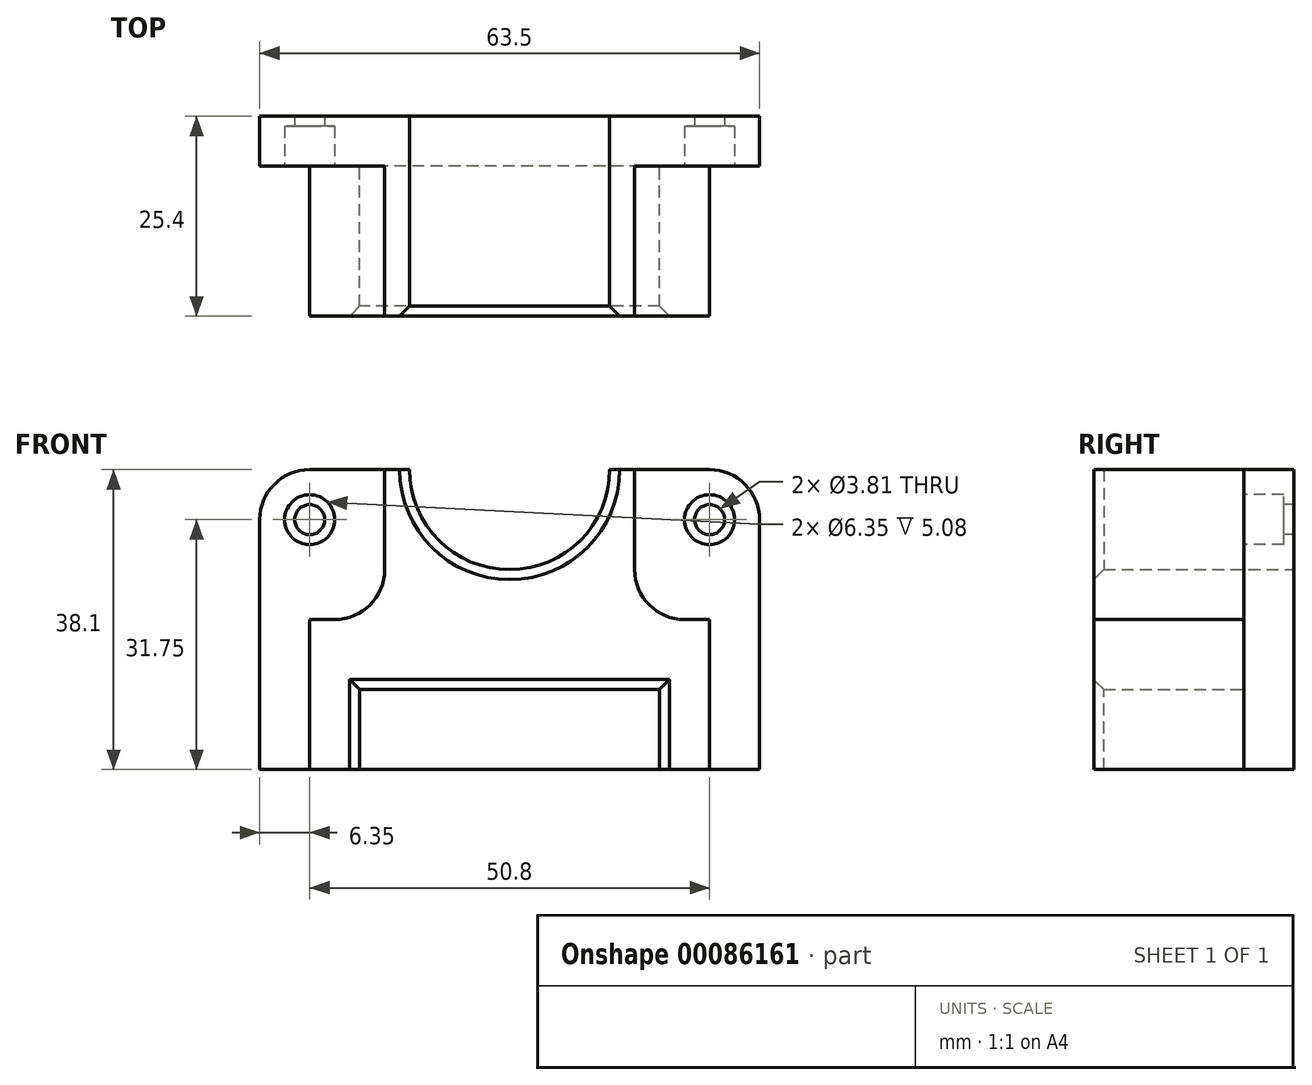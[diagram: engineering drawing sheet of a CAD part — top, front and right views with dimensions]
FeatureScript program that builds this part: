
annotation { "Feature Type Name" : "Feature", "Feature Type Description" : "" }
export const myFeature = defineFeature(function(context is Context, id is Id, definition is map)
    precondition{}
    {
        {
            var Q0;
            Q0=qCreatedBy(makeId("Front.planeOp"),FACE);
            var sketch = newSketch(context, id + "F0", { "sketchPlane" : qUnion([Q0])});
            skLineSegment(sketch, "E0.bottom", {"start": v(25.4, 19.05) * mm, "end": v(-25.4, 19.05) * mm});
            skLineSegment(sketch, "E0.top", {"start": v(31.75, -19.05) * mm, "end": v(-31.75, -19.05) * mm});
            skLineSegment(sketch, "E0.left", {"start": v(31.75, 12.7) * mm, "end": v(31.75, -19.05) * mm});
            skLineSegment(sketch, "E0.right", {"start": v(-31.75, 12.7) * mm, "end": v(-31.75, -19.05) * mm});
            skPoint(sketch, "E0.middle", {"position": v(0, 0) * mm});
            skPoint(sketch, "E1.visualSharp", {"position": v(31.75, 19.05) * mm});
            skArc(sketch, "E1.filletArc", {"start": v(31.75, 12.7) * mm, "mid": v(29.9, 17.2) * mm, "end": v(25.4, 19.05) * mm});
            skPoint(sketch, "E2.visualSharp", {"position": v(-31.75, 19.05) * mm});
            skArc(sketch, "E2.filletArc", {"start": v(-25.4, 19.05) * mm, "mid": v(-29.9, 17.2) * mm, "end": v(-31.75, 12.7) * mm});
            skSolve(sketch);
        }
        {
            var Q0;
            Q0=makeQuery(id+"F0.imprint","IMPRINT",FACE,{"disambiguationData":[TD([[makeQuery(id+"F0.imprint","IMPRINT",EDGE,{"derivedFrom":sQuery(id+"F0.wireOp",EDGE,"E0.bottom")}),1.0]])]});
            extrude(context, id + "F1", {"entities" : qUnion([Q0]), "depth" : 6.35 * mm});
        }
        {
            var Q0;
            Q0=makeQuery(id+"F1.opExtrude","CAP_FACE",FACE,{"disambiguationData":[OSD([sQuery(id+"F0.wireOp",EDGE,"E0.bottom"),sQuery(id+"F0.wireOp",EDGE,"E0.top"),sQuery(id+"F0.wireOp",EDGE,"E0.left"),sQuery(id+"F0.wireOp",EDGE,"E0.right")])],"isStart":false});
            var sketch = newSketch(context, id + "F2", { "sketchPlane" : qUnion([Q0])});
            skLineSegment(sketch, "E3.bottom", {"start": v(25.4, -19.05) * mm, "end": v(19.05, -19.05) * mm});
            skLineSegment(sketch, "E3.top", {"start": v(15.88, 19.05) * mm, "end": v(12.7, 19.05) * mm});
            skLineSegment(sketch, "E3.left", {"start": v(25.4, -19.05) * mm, "end": v(25.4, 0) * mm});
            skLineSegment(sketch, "E3.right", {"start": v(-25.4, -19.05) * mm, "end": v(-25.4, 0) * mm});
            skPoint(sketch, "E3.middle", {"position": v(0, 0) * mm});
            skLineSegment(sketch, "E4.top", {"start": v(19.05, -8.89) * mm, "end": v(-19.05, -8.9) * mm});
            skLineSegment(sketch, "E4.left", {"start": v(19.05, -19.05) * mm, "end": v(19.05, -8.89) * mm});
            skLineSegment(sketch, "E4.right", {"start": v(-19.05, -19.05) * mm, "end": v(-19.05, -8.9) * mm});
            skPoint(sketch, "E4.middle", {"position": v(0, -13.97) * mm});
            skArc(sketch, "E5", {"start": v(-12.7, 19.05) * mm, "mid": v(0, 6.35) * mm, "end": v(12.7, 19.05) * mm});
            skLineSegment(sketch, "E6.top", {"start": v(25.4, 0) * mm, "end": v(22.23, 0) * mm});
            skLineSegment(sketch, "E6.right", {"start": v(15.88, 19.05) * mm, "end": v(15.88, 6.35) * mm});
            skLineSegment(sketch, "E7.top", {"start": v(-25.4, 0) * mm, "end": v(-22.23, 0) * mm});
            skLineSegment(sketch, "E7.right", {"start": v(-15.88, 19.05) * mm, "end": v(-15.88, 6.35) * mm});
            skLineSegment(sketch, "E8.trimOffspring", {"start": v(-19.05, -19.05) * mm, "end": v(-25.4, -19.05) * mm});
            skPoint(sketch, "E9.orphan", {"position": v(25.4, 19.05) * mm});
            skPoint(sketch, "E10.orphan", {"position": v(-25.4, 19.05) * mm});
            skPoint(sketch, "E11.visualSharp", {"position": v(15.88, 0) * mm});
            skArc(sketch, "E11.filletArc", {"start": v(15.88, 6.35) * mm, "mid": v(17.73, 1.86) * mm, "end": v(22.23, 0) * mm});
            skPoint(sketch, "E12.visualSharp", {"position": v(-15.88, 0) * mm});
            skArc(sketch, "E12.filletArc", {"start": v(-22.23, 0) * mm, "mid": v(-17.73, 1.86) * mm, "end": v(-15.88, 6.35) * mm});
            skLineSegment(sketch, "E13.trimOffspring", {"start": v(-12.7, 19.05) * mm, "end": v(-15.87, 19.05) * mm});
            skSolve(sketch);
        }
        {
            var Q0;
            Q0 = qSketchRegion(id + "F2", true);
            extrude(context, id + "F3", {"entities" : qUnion([Q0]), "operationType" : NewBodyOperationType.ADD, "depth" : 19.05 * mm});
        }
        {
            var Q0;
            {var subQ0=sQuery(id+"F0.wireOp",EDGE,"E0.bottom");Q0=makeQuery(id+"F3.boolean.opBoolean","SPLIT",FACE,{"disambiguationData":[TD([makeQuery(id+"F3.opExtrude","SWEPT_FACE",FACE,{"disambiguationData":[OSD([sQuery(id+"F2.wireOp",EDGE,"E5")])]})])],"derivedFrom":makeQuery(id+"F1.opExtrude","CAP_FACE",FACE,{"disambiguationData":[OSD([subQ0,sQuery(id+"F0.wireOp",EDGE,"E0.top"),sQuery(id+"F0.wireOp",EDGE,"E0.left"),sQuery(id+"F0.wireOp",EDGE,"E0.right")])],"isStart":false})});}
            extrude(context, id + "F4", {"entities" : qUnion([Q0]), "operationType" : NewBodyOperationType.REMOVE, "endBound" : BoundingType.THROUGH_ALL, "oppositeDirection" : true, "depth" : 25.4 * mm});
        }
        {
            var Q0;
            Q0=makeQuery(id+"F3.opExtrude","CAP_EDGE",EDGE,{"disambiguationData":[OSD([sQuery(id+"F2.wireOp",EDGE,"E4.top")])],"isStart":false});
            var Q1;
            Q1=makeQuery(id+"F3.opExtrude","CAP_EDGE",EDGE,{"disambiguationData":[OSD([sQuery(id+"F2.wireOp",EDGE,"E4.right")])],"isStart":false});
            var Q2;
            Q2=makeQuery(id+"F3.opExtrude","CAP_EDGE",EDGE,{"disambiguationData":[OSD([sQuery(id+"F2.wireOp",EDGE,"E4.left")])],"isStart":false});
            chamfer(context, id + "F5", {"entities" : qUnion([Q0, Q1, Q2]), "width" : 1.27 * mm, "tangentPropagation" : true});
        }
        {
            var Q0;
            Q0=makeQuery(id+"F3.opExtrude","CAP_EDGE",EDGE,{"disambiguationData":[OSD([sQuery(id+"F2.wireOp",EDGE,"E5")])],"isStart":false});
            chamfer(context, id + "F6", {"entities" : qUnion([Q0]), "width" : 1.27 * mm, "tangentPropagation" : true});
        }
        {
            var Q0;
            {var subQ0=sQuery(id+"F0.wireOp",EDGE,"E0.bottom");var subQ1=sQuery(id+"F0.wireOp",EDGE,"E0.top");var subQ2=sQuery(id+"F0.wireOp",EDGE,"E0.right");var subQ3=sQuery(id+"F0.wireOp",EDGE,"E2.filletArc");Q0=makeQuery(id+"F3.boolean.opBoolean","SPLIT",FACE,{"disambiguationData":[TD([makeQuery(id+"F1.opExtrude","SWEPT_FACE",FACE,{"disambiguationData":[OSD([subQ2])]})])],"derivedFrom":makeQuery(id+"F1.opExtrude","CAP_FACE",FACE,{"disambiguationData":[OSD([subQ0,subQ1,sQuery(id+"F0.wireOp",EDGE,"E0.left"),subQ2,sQuery(id+"F0.wireOp",EDGE,"E1.filletArc"),subQ3])],"isStart":false})});}
            var sketch = newSketch(context, id + "F7", { "sketchPlane" : qUnion([Q0])});
            skPoint(sketch, "E14", {"position": v(-25.4, 12.7) * mm});
            skSolve(sketch);
        }
        {
            var Q0;
            {var subQ0=sQuery(id+"F0.wireOp",EDGE,"E1.filletArc");var subQ1=sQuery(id+"F0.wireOp",EDGE,"E0.left");var subQ2=sQuery(id+"F0.wireOp",EDGE,"E0.bottom");var subQ3=sQuery(id+"F0.wireOp",EDGE,"E0.top");Q0=makeQuery(id+"F3.boolean.opBoolean","SPLIT",FACE,{"disambiguationData":[TD([makeQuery(id+"F1.opExtrude","SWEPT_FACE",FACE,{"disambiguationData":[OSD([subQ1])]})])],"derivedFrom":makeQuery(id+"F1.opExtrude","CAP_FACE",FACE,{"disambiguationData":[OSD([subQ2,subQ3,subQ1,sQuery(id+"F0.wireOp",EDGE,"E0.right"),subQ0,sQuery(id+"F0.wireOp",EDGE,"E2.filletArc")])],"isStart":false})});}
            var sketch = newSketch(context, id + "F8", { "sketchPlane" : qUnion([Q0])});
            skPoint(sketch, "E15", {"position": v(25.4, 12.7) * mm});
            skSolve(sketch);
        }
        {
            var Q0;
            Q0=sQuery(id+"F7.wireOp",VERTEX,"E14");
            var Q1;
            Q1=sQuery(id+"F8.wireOp",VERTEX,"E15");
            var Q2;
            Q2=makeQuery(id+"F1.opExtrude","SWEPT_BODY",BODY,{"disambiguationData":[OSD([sQuery(id+"F0.wireOp",EDGE,"E0.bottom"),sQuery(id+"F0.wireOp",EDGE,"E0.top"),sQuery(id+"F0.wireOp",EDGE,"E0.left"),sQuery(id+"F0.wireOp",EDGE,"E0.right"),sQuery(id+"F0.wireOp",EDGE,"E1.filletArc"),sQuery(id+"F0.wireOp",EDGE,"E2.filletArc")])]});
            hole(context, id + "F9", {"style" : HoleStyle.C_BORE, "endStyle" : HoleEndStyle.THROUGH, "holeDiameter" : 3.8 * mm, "cBoreDiameter" : 6.35 * mm, "cBoreDepth" : 5.08 * mm, "startFromSketch" : true, "locations" : qUnion([Q0, Q1]), "scope" : qUnion([Q2]), "isTappedThrough" : true});
        }
    });
